# Revit family: QSTS
name_source: partatom
category: Mechanical Equipment
revit_build: Autodesk Revit 2018 (Build: 20170223_1515(x64)
units: mm (PartAtom-declared; Revit-internal decimal feet)

## family parameters
Always vertical = Yes
Cut with Voids When Loaded = No
Part Type = Normal
Room Calculation Point = No
Round Connector Dimension = Use Radius
Shared = No
Work Plane-Based = No

## types (28) — shared parameters
Description = Series Fan Powered Air Terminal
Manufacturer = Anemostat
Model = QSTS
URL = http://www.anemostat.com

## per-type parameters (varying)
| type | Diameter | Discharge Height "Y" | Discharge Width "X" | Duct Inlet | Height | Induction | Induction Width "C" | Length | Q5 Sound Elbow | Q5A | Q5B | Q5Q | Radius | Width |
| QSTS 1/2-hp - 10" with S/Elbow | 9 7/8" | 12" | 14" | 5" | 18" | No | 17" | 40" | Yes | 18" | 20" | 18" | 4 15/16" | 40" |
| QSTS 1/2-hp - 10" W/Out S/Elbow | 9 7/8" | 12" | 14" | 5" | 18" | Yes | 17" | 40" | No | 18" | 20" | 18" | 4 15/16" | 40" |
| QSTS 1/2-hp - 12" with S/Elbow | 11 7/8" | 12" | 14" | 6" | 18" | No | 17" | 40" | Yes | 18" | 20" | 18" | 5 15/16" | 40" |
| QSTS 1/2-hp - 12" W/Out S/Elbow | 11 7/8" | 12" | 14" | 6" | 18" | Yes | 17" | 40" | No | 18" | 20" | 18" | 5 15/16" | 40" |
| QSTS 1/2-hp - 14" with S/Elbow | 13 7/8" | 12" | 14" | 7" | 18" | No | 17" | 40" | Yes | 18" | 20" | 18" | 6 15/16" | 40" |
| QSTS 1/2-hp - 14" W/Out S/Elbow | 13 7/8" | 12" | 14" | 7" | 18" | Yes | 17" | 40" | No | 18" | 20" | 18" | 6 15/16" | 40" |
| QSTS 1-hp - 12" with S/Elbow | 11 7/8" | 16" | 19" | 6" | 20" | No | 21" | 48" | Yes | 20" | 24" | 20" | 5 15/16" | 48" |
| QSTS 3/4-hp - 12" W/Out S/Elbow | 11 7/8" | 16" | 19" | 6" | 20" | Yes | 21" | 48" | No | 20" | 24" | 20" | 5 15/16" | 48" |
| QSTS 3/4-hp - 14" with S/Elbow | 14 7/8" | 16" | 19" | 7" | 20" | No | 21" | 48" | Yes | 20" | 24" | 20" | 7 7/16" | 48" |
| QSTS 3/4-hp - 14" W/Out S/Elbow | 14 7/8" | 16" | 19" | 7" | 20" | Yes | 21" | 48" | No | 20" | 24" | 20" | 7 7/16" | 48" |
| QSTS 1-hp - 16" W/Out S/Elbow | 15 7/8" | 16" | 19" | 8" | 20" | Yes | 21" | 48" | No | 20" | 24" | 20" | 7 15/16" | 48" |
| QSTS 1-hp - 16" with S/Elbow | 15 7/8" | 16" | 19" | 8" | 20" | No | 21" | 48" | Yes | 20" | 24" | 20" | 7 15/16" | 48" |
| QSTS 1-hp - 14" W/Out S/Elbow | 14 7/8" | 16" | 19" | 7" | 20" | Yes | 21" | 48" | No | 20" | 24" | 20" | 7 7/16" | 48" |
| QSTS 1-hp - 14" with S/Elbow | 14 7/8" | 16" | 19" | 7" | 20" | No | 21" | 48" | Yes | 20" | 24" | 20" | 7 7/16" | 48" |
| QSTS 1-hp - 12" W/Out S/Elbow | 11 7/8" | 16" | 19" | 6" | 20" | Yes | 21" | 48" | No | 20" | 24" | 20" | 5 15/16" | 48" |
| QSTS 3/4-hp - 12" with S/Elbow | 11 7/8" | 16" | 19" | 6" | 20" | No | 21" | 48" | Yes | 20" | 24" | 20" | 5 15/16" | 48" |
| QSTS 1/4-hp - 08" W/Out S/Elbow | 7 7/8" | 11" | 11 1/2" | 4" | 18" | Yes | 12" | 36" | No | 18" | 18" | 18" | 3 15/16" | 32" |
| QSTS 1/4-hp - 08" with S/Elbow | 7 7/8" | 11" | 11 1/2" | 4" | 18" | No | 12" | 36" | Yes | 18" | 18" | 18" | 3 15/16" | 32" |
| QSTS 1/4-hp - 09" W/Out S/Elbow | 8 7/8" | 11" | 11 1/2" | 4" | 18" | Yes | 12" | 36" | No | 18" | 18" | 18" | 4 7/16" | 32" |
| QSTS 1/4-hp - 09" with S/Elbow | 8 7/8" | 11" | 11 1/2" | 4" | 18" | No | 12" | 36" | Yes | 18" | 18" | 18" | 4 7/16" | 32" |
| QSTS 1/4-hp - 10" W/Out S/Elbow | 9 7/8" | 11" | 11 1/2" | 5" | 18" | Yes | 12" | 36" | No | 18" | 18" | 18" | 4 15/16" | 32" |
| QSTS 1/4-hp - 10" with S/Elbow | 9 7/8" | 11" | 11 1/2" | 5" | 18" | No | 12" | 36" | Yes | 18" | 18" | 18" | 4 15/16" | 32" |
| QSTS 1/6-hp - 06" W/Out S/Elbow | 5 7/8" | 11" | 11 1/2" | 3" | 18" | Yes | 12" | 36" | No | 18" | 18" | 18" | 2 15/16" | 32" |
| QSTS 1/6-hp - 06" with S/Elbow | 5 7/8" | 11" | 11 1/2" | 3" | 18" | No | 12" | 36" | Yes | 18" | 18" | 18" | 2 15/16" | 32" |
| QSTS 1/6-hp - 07" W/Out S/Elbow | 6 7/8" | 11" | 11 1/2" | 3" | 18" | Yes | 12" | 36" | No | 18" | 18" | 18" | 3 7/16" | 32" |
| QSTS 1/6-hp - 07" with S/Elbow | 6 7/8" | 11" | 11 1/2" | 3" | 18" | No | 12" | 36" | Yes | 18" | 18" | 18" | 3 7/16" | 32" |
| QSTS 1/6-hp - 08" with S/Elbow | 7 7/8" | 11" | 11 1/2" | 4" | 18" | No | 12" | 36" | Yes | 18" | 18" | 18" | 3 15/16" | 32" |
| QSTS 1/6-hp - 08" W/Out S/Elbow | 7 7/8" | 11" | 11 1/2" | 4" | 18" | Yes | 12" | 36" | No | 18" | 18" | 18" | 3 15/16" | 32" |

## geometry (parser evidence)
native form markers: Sweep x2
no freeform markers — native parametric forms only
